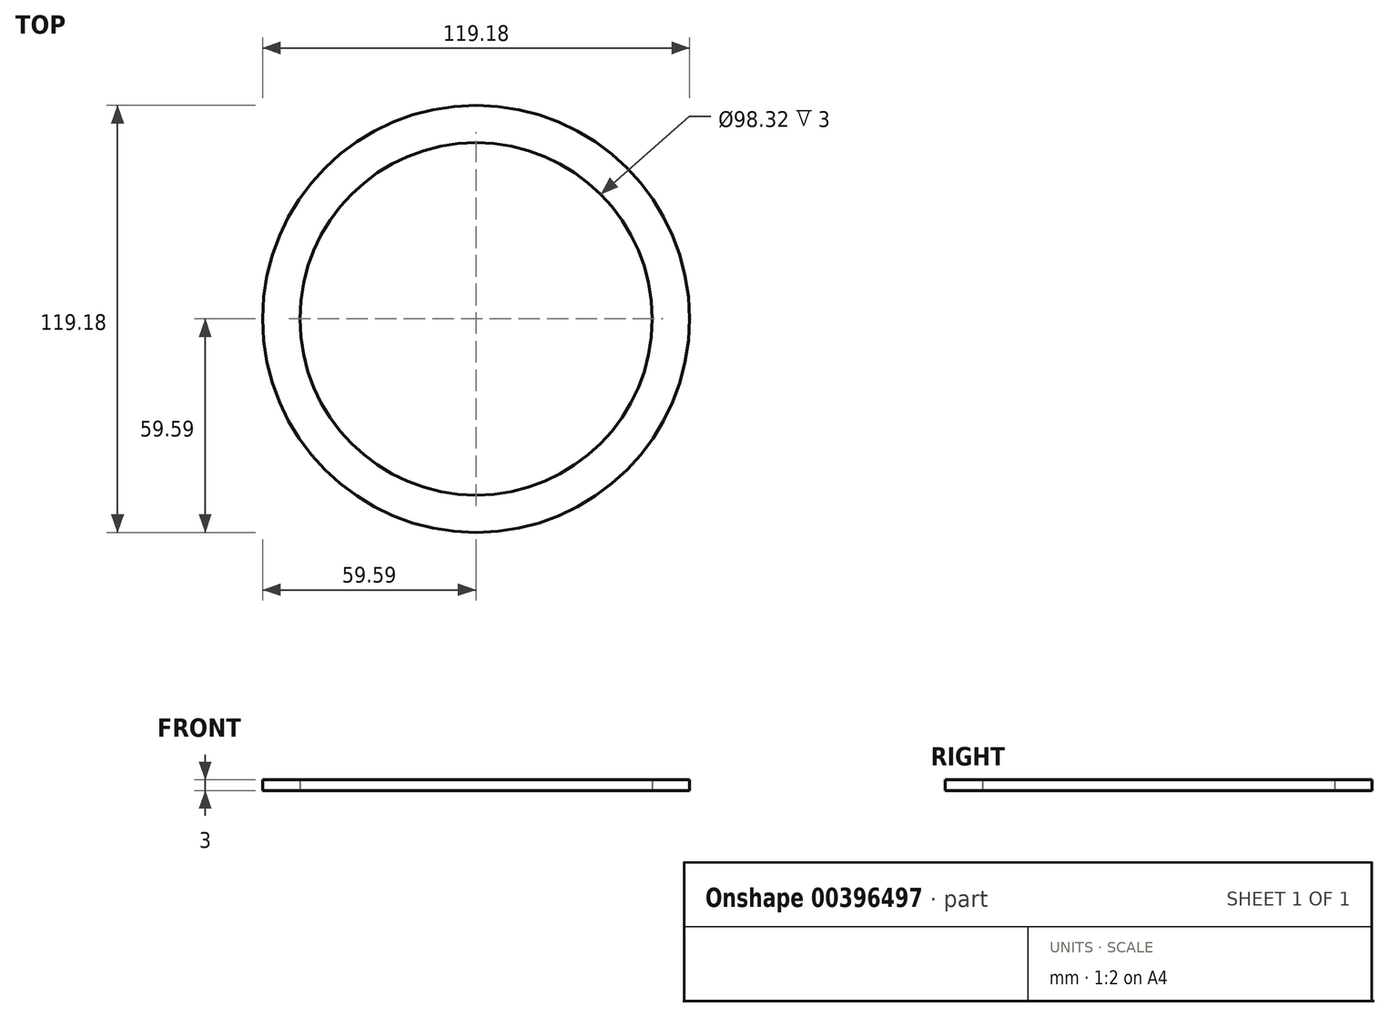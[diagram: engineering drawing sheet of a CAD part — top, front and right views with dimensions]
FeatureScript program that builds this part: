
annotation { "Feature Type Name" : "Feature", "Feature Type Description" : "" }
export const myFeature = defineFeature(function(context is Context, id is Id, definition is map)
    precondition{}
    {
        {
            var Q0;
            Q0=qCreatedBy(makeId("Top.planeOp"),FACE);
            var sketch = newSketch(context, id + "F0", { "sketchPlane" : qUnion([Q0])});
            skCircle(sketch, "E0", {"center": v(0, 0) * mm, "radius": 59.59 * mm});
            skCircle(sketch, "E1", {"center": v(0, 0) * mm, "radius": 49.16 * mm});
            skSolve(sketch);
        }
        {
            var Q0;
            Q0=makeQuery(id+"F0.imprint","IMPRINT",FACE,{"disambiguationData":[TD([[makeQuery(id+"F0.imprint","IMPRINT",EDGE,{"derivedFrom":sQuery(id+"F0.wireOp",EDGE,"E0")}),1.0]])]});
            extrude(context, id + "F1", {"entities" : qUnion([Q0]), "depth" : 3 * mm});
        }
    });
